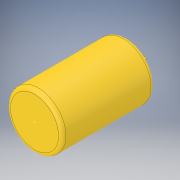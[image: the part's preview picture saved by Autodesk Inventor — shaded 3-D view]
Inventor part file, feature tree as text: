
AUTODESK INVENTOR PART (.ipt)
format: ipt  version: 2019 (Build 230136000, 136)  size: 138,752 bytes
history: native  units: in
note: dims shown in document units (in); Inventor stores cm internally (conversion verified against a paired STEP export)
features: sketch x4, extrude x3, fillet x1
ambient origin geometry x8: Origin, YZ Plane, XZ Plane, XY Plane, X Axis, Y Axis, Z Axis, Center Point
bodies: Solid1 (feature_tree)
feature tree (8):
  extrude  "Extrusion1"  Depth=1.9685in TaperAngle=0.0deg
  sketch  "Sketch2"  dims[d3=0.1969in d4=0.2362in d5=0.1969in d6=0.0in]
  extrude  "Extrusion2"  Depth=0.2362in
  fillet  "Fillet1"  Radius=0.1969in
  extrude  "Extrusion3"  Depth=0.0787in
  sketch  "Sketch1"  dims[d0=1.1811in d1=1.9685in d2=0.0in]
  sketch  "Sketch3"  dims[d7=0.0787in d8=0.0394in]
  sketch  "Sketch4"  dims[d9=0.3937in d10=0.0in]
